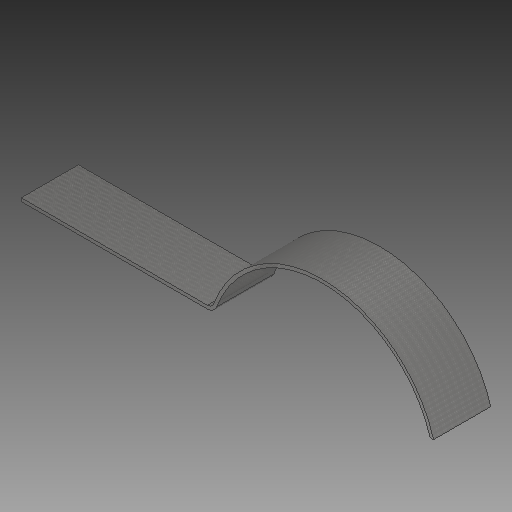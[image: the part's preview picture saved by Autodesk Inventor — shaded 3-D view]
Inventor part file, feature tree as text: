
AUTODESK INVENTOR PART (.ipt)
format: ipt  version: 2019 (Build 230136000, 136)  size: 136,704 bytes
history: native  units: mm
features: extrude x1, sketch x1
ambient origin geometry x8: Origin, YZ Plane, XZ Plane, XY Plane, X Axis, Y Axis, Z Axis, Center Point
bodies: Solid1 (feature_tree)
feature tree (2):
  extrude  "Extrusion1"  Depth=345.0mm
  sketch  "Sketch1"  dims[d23=175.0mm d24=0.0mm d25=130.0mm d26=20.0mm d27=30.0mm d28=570.0mm d29=345.0mm d30=100.0mm]
